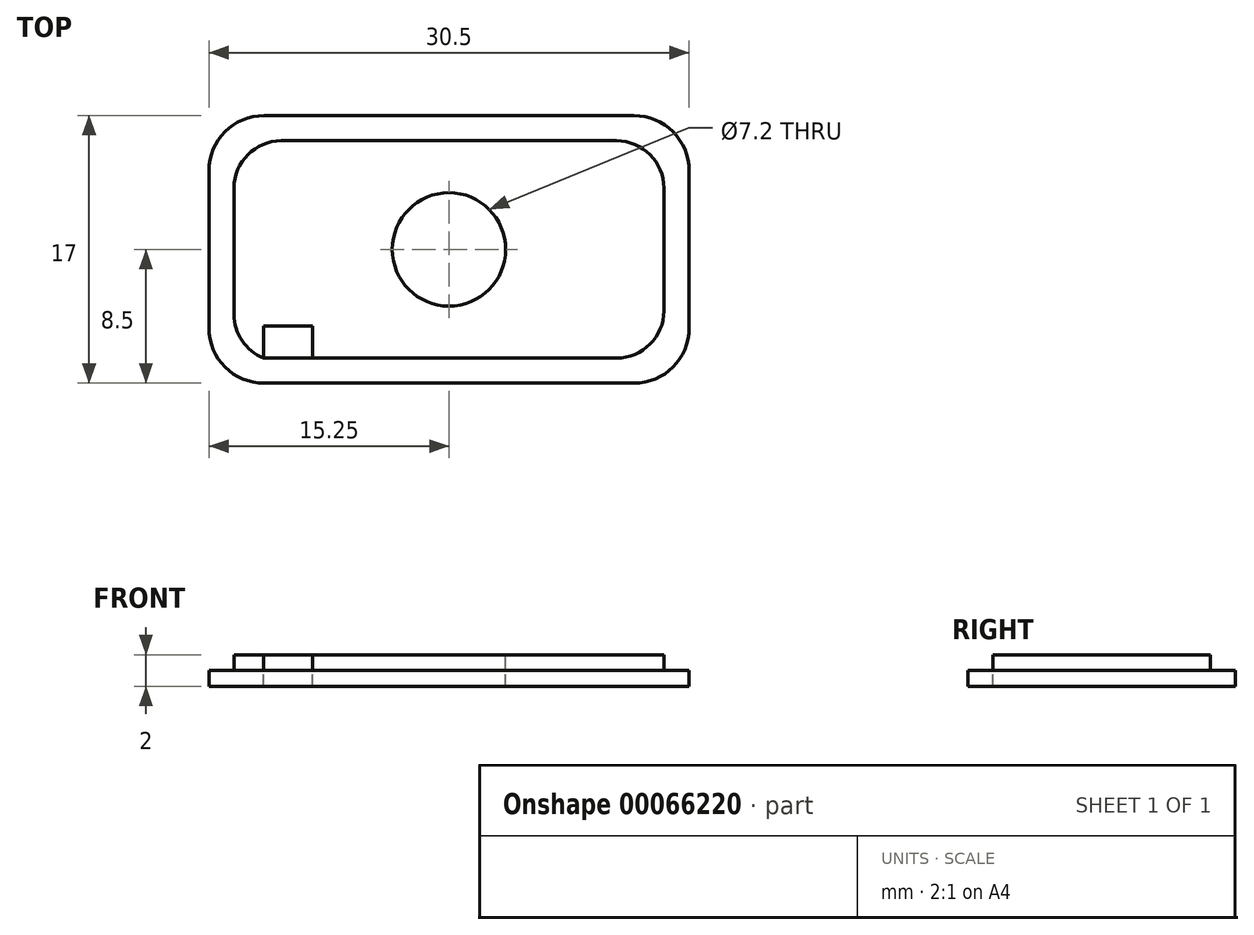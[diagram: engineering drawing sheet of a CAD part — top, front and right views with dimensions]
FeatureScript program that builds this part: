
annotation { "Feature Type Name" : "Feature", "Feature Type Description" : "" }
export const myFeature = defineFeature(function(context is Context, id is Id, definition is map)
    precondition{}
    {
        {
            var Q0;
            Q0=qCreatedBy(makeId("Top.planeOp"),FACE);
            var sketch = newSketch(context, id + "F0", { "sketchPlane" : qUnion([Q0])});
            skLineSegment(sketch, "E0.rect.bottom", {"start": v(15.25, 8.5) * mm, "end": v(-15.25, 8.5) * mm});
            skLineSegment(sketch, "E0.rect.top", {"start": v(15.25, -8.5) * mm, "end": v(-15.25, -8.5) * mm});
            skLineSegment(sketch, "E0.rect.left", {"start": v(15.25, 8.5) * mm, "end": v(15.25, -8.5) * mm});
            skLineSegment(sketch, "E0.rect.right", {"start": v(-15.25, 8.5) * mm, "end": v(-15.25, -8.5) * mm});
            skPoint(sketch, "E0.rect.middle", {"position": v(0, 0) * mm});
            skSolve(sketch);
        }
        {
            var Q0;
            Q0=qSketchRegion(id+"F0",true);
            extrude(context, id + "F1", {"entities" : qUnion([Q0]), "depth" : 1 * mm});
        }
        {
            var Q0;
            Q0=makeQuery(id+"F1.opExtrude","CAP_FACE",FACE,{"disambiguationData":[OSD([sQuery(id+"F0.wireOp",EDGE,"E0.rect.bottom"),sQuery(id+"F0.wireOp",EDGE,"E0.rect.top"),sQuery(id+"F0.wireOp",EDGE,"E0.rect.left"),sQuery(id+"F0.wireOp",EDGE,"E0.rect.right")])],"isStart":false});
            var sketch = newSketch(context, id + "F2", { "sketchPlane" : qUnion([Q0])});
            skLineSegment(sketch, "E1.rect.bottom", {"start": v(13.65, 6.9) * mm, "end": v(-13.65, 6.9) * mm});
            skLineSegment(sketch, "E1.rect.top", {"start": v(13.65, -6.9) * mm, "end": v(-13.65, -6.9) * mm});
            skLineSegment(sketch, "E1.rect.left", {"start": v(13.65, 6.9) * mm, "end": v(13.65, -6.9) * mm});
            skLineSegment(sketch, "E1.rect.right", {"start": v(-13.65, 6.9) * mm, "end": v(-13.65, -6.9) * mm});
            skPoint(sketch, "E1.rect.middle", {"position": v(0, 0) * mm});
            skSolve(sketch);
        }
        {
            var Q0;
            Q0=qSketchRegion(id+"F2",true);
            extrude(context, id + "F3", {"entities" : qUnion([Q0]), "operationType" : NewBodyOperationType.ADD, "depth" : 1 * mm});
        }
        {
            var Q0;
            Q0=makeQuery(id+"F3.opExtrude","CAP_FACE",FACE,{"disambiguationData":[OSD([sQuery(id+"F2.wireOp",EDGE,"E1.rect.bottom"),sQuery(id+"F2.wireOp",EDGE,"E1.rect.top"),sQuery(id+"F2.wireOp",EDGE,"E1.rect.left"),sQuery(id+"F2.wireOp",EDGE,"E1.rect.right")])],"isStart":false});
            var sketch = newSketch(context, id + "F4", { "sketchPlane" : qUnion([Q0])});
            skCircle(sketch, "E2", {"center": v(0, 0) * mm, "radius": 3.6 * mm});
            skLineSegment(sketch, "E3", {"start": v(13.65, -6.9) * mm, "end": v(-8.68, -6.9) * mm, "construction": true});
            skLineSegment(sketch, "E4", {"start": v(-8.68, -6.9) * mm, "end": v(-8.68, -4.88) * mm, "construction": true});
            skLineSegment(sketch, "E5", {"start": v(-8.68, -4.88) * mm, "end": v(-11.78, -4.88) * mm, "construction": true});
            skLineSegment(sketch, "E6.bottom", {"start": v(-11.78, -4.88) * mm, "end": v(-8.68, -4.88) * mm});
            skLineSegment(sketch, "E6.top", {"start": v(-11.78, -6.9) * mm, "end": v(-8.68, -6.9) * mm});
            skLineSegment(sketch, "E6.left", {"start": v(-11.78, -4.88) * mm, "end": v(-11.78, -6.9) * mm});
            skLineSegment(sketch, "E6.right", {"start": v(-8.68, -4.88) * mm, "end": v(-8.68, -6.9) * mm});
            skSolve(sketch);
        }
        {
            var Q0;
            Q0=qSketchRegion(id+"F4",true);
            extrude(context, id + "F5", {"entities" : qUnion([Q0]), "operationType" : NewBodyOperationType.REMOVE, "oppositeDirection" : true, "depth" : 2 * mm});
        }
        {
            var Q0;
            Q0=makeQuery(id+"F3.opExtrude","SWEPT_EDGE",EDGE,{"disambiguationData":[OSD([sQuery(id+"F2.wireOp",EDGE,"E1.rect.top"),sQuery(id+"F2.wireOp",EDGE,"E1.rect.right")])]});
            var Q1;
            Q1=makeQuery(id+"F3.opExtrude","SWEPT_EDGE",EDGE,{"disambiguationData":[OSD([sQuery(id+"F2.wireOp",EDGE,"E1.rect.top"),sQuery(id+"F2.wireOp",EDGE,"E1.rect.left")])]});
            var Q2;
            Q2=makeQuery(id+"F3.opExtrude","SWEPT_EDGE",EDGE,{"disambiguationData":[OSD([sQuery(id+"F2.wireOp",EDGE,"E1.rect.bottom"),sQuery(id+"F2.wireOp",EDGE,"E1.rect.right")])]});
            var Q3;
            Q3=makeQuery(id+"F3.opExtrude","SWEPT_EDGE",EDGE,{"disambiguationData":[OSD([sQuery(id+"F2.wireOp",EDGE,"E1.rect.bottom"),sQuery(id+"F2.wireOp",EDGE,"E1.rect.left")])]});
            fillet(context, id + "F6", {"entities" : qUnion([Q0, Q1, Q2, Q3]), "radius" : 3 * mm, "tangentPropagation" : true, "allowEdgeOverflow" : false});
        }
        {
            var Q0;
            Q0=makeQuery(id+"F1.opExtrude","SWEPT_EDGE",EDGE,{"disambiguationData":[OSD([sQuery(id+"F0.wireOp",EDGE,"E0.rect.bottom"),sQuery(id+"F0.wireOp",EDGE,"E0.rect.left")])]});
            var Q1;
            Q1=makeQuery(id+"F1.opExtrude","SWEPT_EDGE",EDGE,{"disambiguationData":[OSD([sQuery(id+"F0.wireOp",EDGE,"E0.rect.bottom"),sQuery(id+"F0.wireOp",EDGE,"E0.rect.right")])]});
            var Q2;
            Q2=makeQuery(id+"F1.opExtrude","SWEPT_EDGE",EDGE,{"disambiguationData":[OSD([sQuery(id+"F0.wireOp",EDGE,"E0.rect.top"),sQuery(id+"F0.wireOp",EDGE,"E0.rect.right")])]});
            var Q3;
            Q3=makeQuery(id+"F1.opExtrude","SWEPT_EDGE",EDGE,{"disambiguationData":[OSD([sQuery(id+"F0.wireOp",EDGE,"E0.rect.top"),sQuery(id+"F0.wireOp",EDGE,"E0.rect.left")])]});
            fillet(context, id + "F7", {"entities" : qUnion([Q0, Q1, Q2, Q3]), "radius" : 3.5 * mm, "tangentPropagation" : true, "allowEdgeOverflow" : false});
        }
    });
